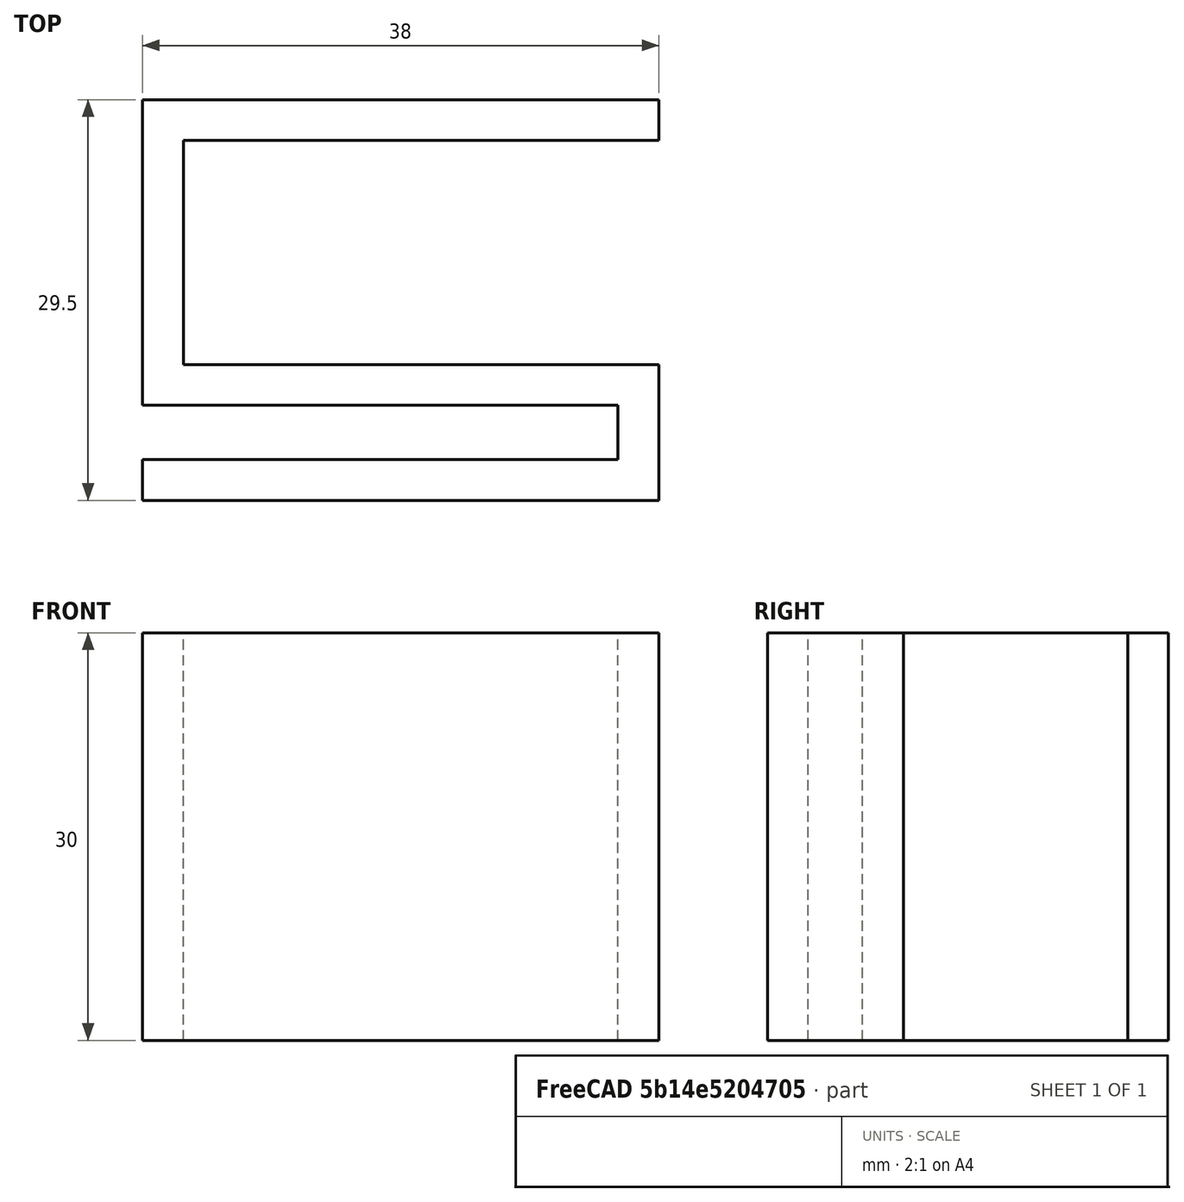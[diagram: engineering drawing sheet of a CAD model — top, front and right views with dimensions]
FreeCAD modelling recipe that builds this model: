
FCSTD DOCUMENT  (FreeCAD 0.21R33771 (Git))
Label: FanClip
License: All rights reserved
LicenseURL: https://en.wikipedia.org/wiki/All_rights_reserved
objects: Sketcher::SketchObject×1, PartDesign::Pad×1, PartDesign::Body×1
note: 4 computed .brp shape members not serialized (recipe doc carries the construction recipe); baked Part::Feature solids carry a one-line shape summary decoded from their .brp

FEATURE [Sketcher::SketchObject] Sketch
  FullyConstrained = true
  MapMode = 5
  Support = -> [XY_Plane]
  sketch-geometry (12):
    g0: LineSegment StartX=38 StartY=29.5 StartZ=0 EndX=0 EndY=29.5 EndZ=0
    g1: LineSegment StartX=0 StartY=29.5 StartZ=0 EndX=0 EndY=7 EndZ=0
    g2: LineSegment StartX=0 StartY=7 StartZ=0 EndX=35 EndY=7 EndZ=0
    g3: LineSegment StartX=35 StartY=7 StartZ=0 EndX=35 EndY=3 EndZ=0
    g4: LineSegment StartX=35 StartY=3 StartZ=0 EndX=0 EndY=3 EndZ=0
    g5: LineSegment StartX=0 StartY=3 StartZ=0 EndX=0 EndY=0 EndZ=0
    g6: LineSegment StartX=0 StartY=0 StartZ=0 EndX=38 EndY=0 EndZ=0
    g7: LineSegment StartX=38 StartY=0 StartZ=0 EndX=38 EndY=10 EndZ=0
    g8: LineSegment StartX=38 StartY=10 StartZ=0 EndX=3 EndY=10 EndZ=0
    g9: LineSegment StartX=3 StartY=10 StartZ=0 EndX=3 EndY=26.5 EndZ=0
    g10: LineSegment StartX=3 StartY=26.5 StartZ=0 EndX=38 EndY=26.5 EndZ=0
    g11: LineSegment StartX=38 StartY=26.5 StartZ=0 EndX=38 EndY=29.5 EndZ=0
  constraints (35):
    c: Horizontal(g0)
    c: Coincident(g0,g1)
    c: Vertical(g1)
    c: Coincident(g1,g2)
    c: Horizontal(g2)
    c: Coincident(g2,g3)
    c: Vertical(g3)
    c: Coincident(g3,g4)
    c: Horizontal(g4)
    c: Coincident(g4,g5)
    c: Vertical(g5)
    c: Coincident(g5,g6)
    c: Horizontal(g6)
    c: Coincident(g6,g7)
    c: Vertical(g7)
    c: Coincident(g7,g8)
    c: Horizontal(g8)
    c: Coincident(g8,g9)
    c: Vertical(g9)
    c: Coincident(g9,g10)
    c: Horizontal(g10)
    c: Coincident(g10,g11)
    c: Coincident(g11,g0)
    c: Vertical(g11)
    c: Distance(g9) = 16.5
    c: Distance(g3) = 4
    c: Distance(g4) = 35
    c: DistanceX(g1,g4) = 0
    c: Distance(g5) = 3
    c: Distance(g11) = 3
    c: DistanceX(g3,g6) = 3
    c: DistanceY(g2,g7) = 3
    c: DistanceX(g0,g9) = 3
    c: Coincident(g5,g-1)
    c: Distance(g10) = 35
FEATURE [PartDesign::Pad] Pad
  Direction = (0,0,1)
  Length = 30
  Length2 = 10
  Profile = -> Sketch
  ReferenceAxis = -> Sketch [N_Axis]
  Type = 0
FEATURE [PartDesign::Body] Body  label="FanClip"
  Group = -> [Sketch,Pad]
  Origin = -> Origin
  Tip = -> Pad
